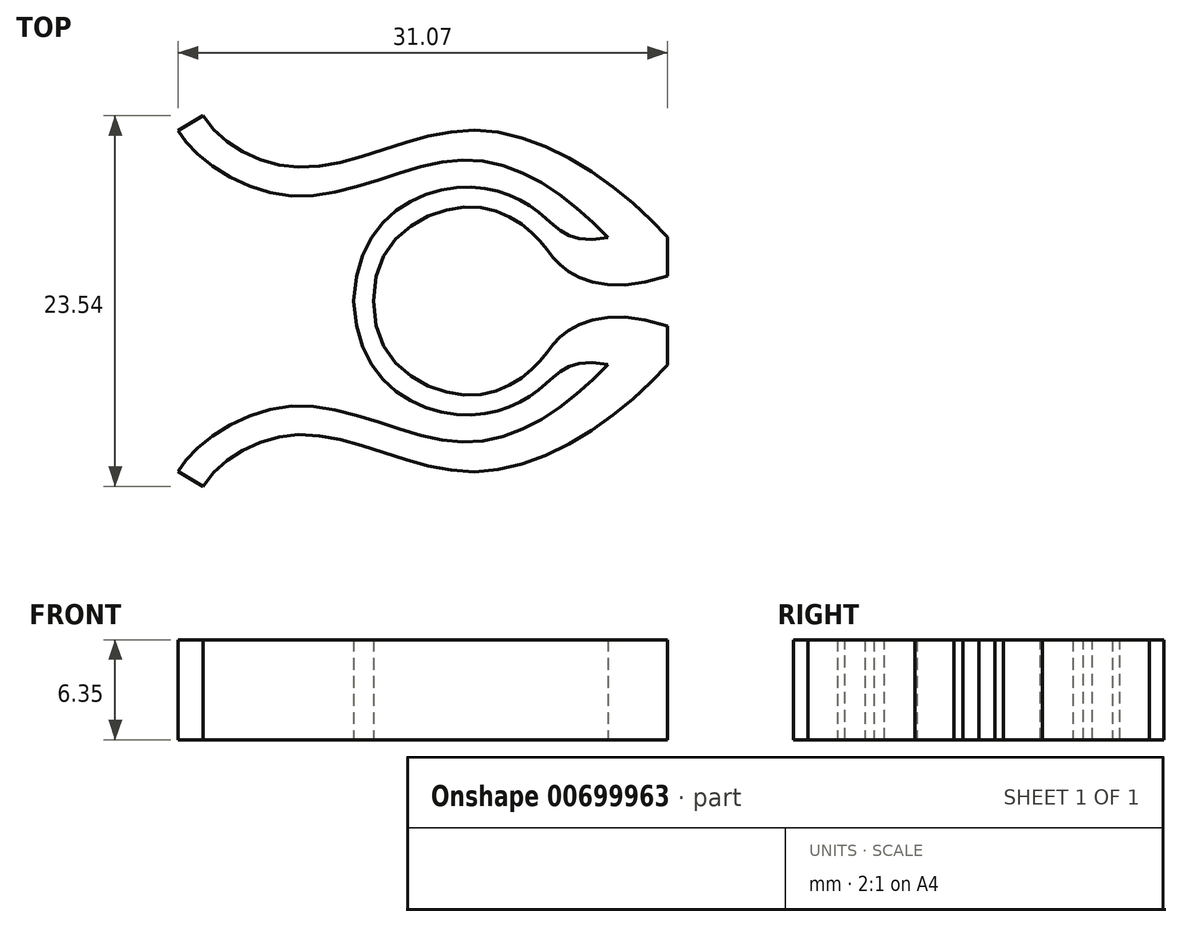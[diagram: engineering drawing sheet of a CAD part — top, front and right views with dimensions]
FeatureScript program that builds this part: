
annotation { "Feature Type Name" : "Feature", "Feature Type Description" : "" }
export const myFeature = defineFeature(function(context is Context, id is Id, definition is map)
    precondition{}
    {
        {
            var Q0;
            Q0=qCreatedBy(makeId("Top.planeOp"),FACE);
            var sketch = newSketch(context, id + "F0", { "sketchPlane" : qUnion([Q0])});
            skCircle(sketch, "E0", {"center": v(0, 0) * mm, "radius": 5.97 * mm, "construction": true});
            skCircle(sketch, "E1", {"center": v(0, 0) * mm, "radius": 7.24 * mm, "construction": true});
            skLineSegment(sketch, "E2.bottom", {"start": v(0, 1.57) * mm, "end": v(12.7, 1.57) * mm, "construction": true});
            skLineSegment(sketch, "E2.top", {"start": v(0, 0) * mm, "end": v(12.7, 0) * mm, "construction": true});
            skLineSegment(sketch, "E2.left", {"start": v(0, 1.57) * mm, "end": v(0, 0) * mm, "construction": true});
            skLineSegment(sketch, "E2.right", {"start": v(12.7, 1.57) * mm, "end": v(12.7, 0) * mm, "construction": true});
            skFitSpline(sketch, "E3", {"points": [v(-5.97, 0) * mm, v(0, 5.97) * mm, v(4.4, 4.02) * mm, v(6.27, 1.98) * mm, v(12.7, 1.57) * mm], "startDerivative": vector(-0.97, 38.29) * mm, "endDerivative": vector(34.44, 11.36) * mm});
            skFitSpline(sketch, "E4", {"points": [v(-7.24, 0) * mm, v(0, 7.24) * mm, v(4.86, 5.37) * mm, v(8.94, 4.03) * mm], "startDerivative": vector(1.78, 38.42) * mm, "endDerivative": vector(26.75, 4.85) * mm});
            skFitSpline(sketch, "E5", {"points": [v(8.94, 4.03) * mm, v(0, 8.97) * mm, v(-11.11, 6.68) * mm, v(-18.37, 10.84) * mm], "startDerivative": vector(-21.35, 22.36) * mm, "endDerivative": vector(-8.21, 16.43) * mm});
            skFitSpline(sketch, "E6", {"points": [v(12.7, 4.06) * mm, v(0.92, 10.83) * mm, v(-10.23, 8.5) * mm, v(-16.78, 11.77) * mm], "startDerivative": vector(-22.2, 24.63) * mm, "endDerivative": vector(-12.96, 20.83) * mm});
            skLineSegment(sketch, "E7", {"start": v(-16.78, 11.77) * mm, "end": v(-18.37, 10.84) * mm});
            skLineSegment(sketch, "E8", {"start": v(12.7, 1.57) * mm, "end": v(12.7, 4.06) * mm});
            skLineSegment(sketch, "E9", {"start": v(-7.24, 0) * mm, "end": v(-5.97, 0) * mm});
            skSolve(sketch);
        }
        {
            var Q0;
            Q0=qSketchRegion(id+"F0",true);
            extrude(context, id + "F1", {"entities" : qUnion([Q0]), "depth" : 6.35 * mm, "offsetDistance" : 25.4 * mm});
        }
        {
            var Q0;
            Q0=makeQuery(id+"F1.opExtrude","SWEPT_BODY",BODY,{"disambiguationData":[OSD([sQuery(id+"F0.wireOp",EDGE,"E3"),sQuery(id+"F0.wireOp",EDGE,"E4"),sQuery(id+"F0.wireOp",EDGE,"E5"),sQuery(id+"F0.wireOp",EDGE,"E6"),sQuery(id+"F0.wireOp",EDGE,"E7"),sQuery(id+"F0.wireOp",EDGE,"E8"),sQuery(id+"F0.wireOp",EDGE,"E9")])]});
            var Q1;
            Q1=qCreatedBy(makeId("Front.planeOp"),FACE);
            mirror(context, id + "F2", {"operationType" : NewBodyOperationType.ADD, "entities" : qUnion([Q0]), "mirrorPlane" : qUnion([Q1])});
        }
    });
